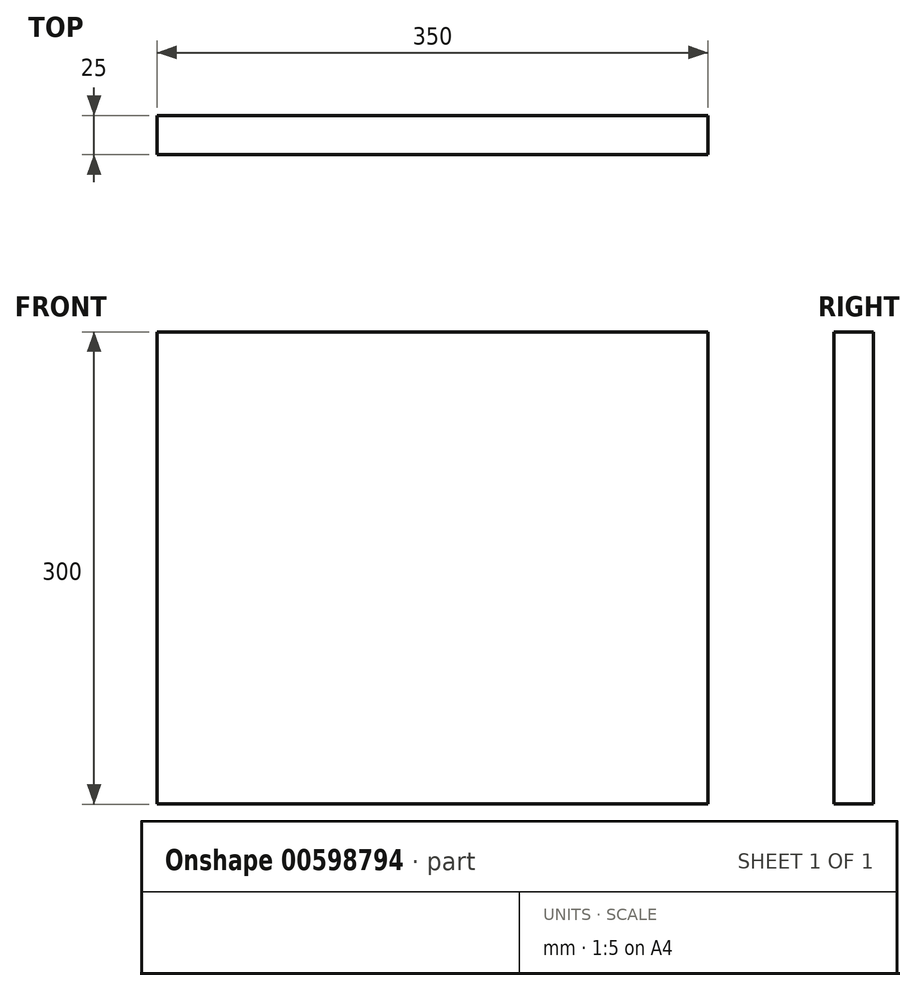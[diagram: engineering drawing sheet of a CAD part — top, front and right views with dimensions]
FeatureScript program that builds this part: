
annotation { "Feature Type Name" : "Feature", "Feature Type Description" : "" }
export const myFeature = defineFeature(function(context is Context, id is Id, definition is map)
    precondition{}
    {
        {
            var Q0;
            Q0=qCreatedBy(makeId("Front.planeOp"),FACE);
            var sketch = newSketch(context, id + "F0", { "sketchPlane" : qUnion([Q0])});
            skLineSegment(sketch, "E0.bottom", {"start": v(-156.45, 195.23) * mm, "end": v(193.55, 195.23) * mm});
            skLineSegment(sketch, "E0.top", {"start": v(-156.45, -104.77) * mm, "end": v(193.55, -104.77) * mm});
            skLineSegment(sketch, "E0.left", {"start": v(-156.45, 195.23) * mm, "end": v(-156.45, -104.77) * mm});
            skLineSegment(sketch, "E0.right", {"start": v(193.55, 195.23) * mm, "end": v(193.55, -104.77) * mm});
            skSolve(sketch);
        }
        {
            var Q0;
            Q0 = qSketchRegion(id + "F0", true);
            extrude(context, id + "F1", {"entities" : qUnion([Q0]), "oppositeDirection" : true, "depth" : 25 * mm, "offsetDistance" : 25 * mm});
        }
    });
